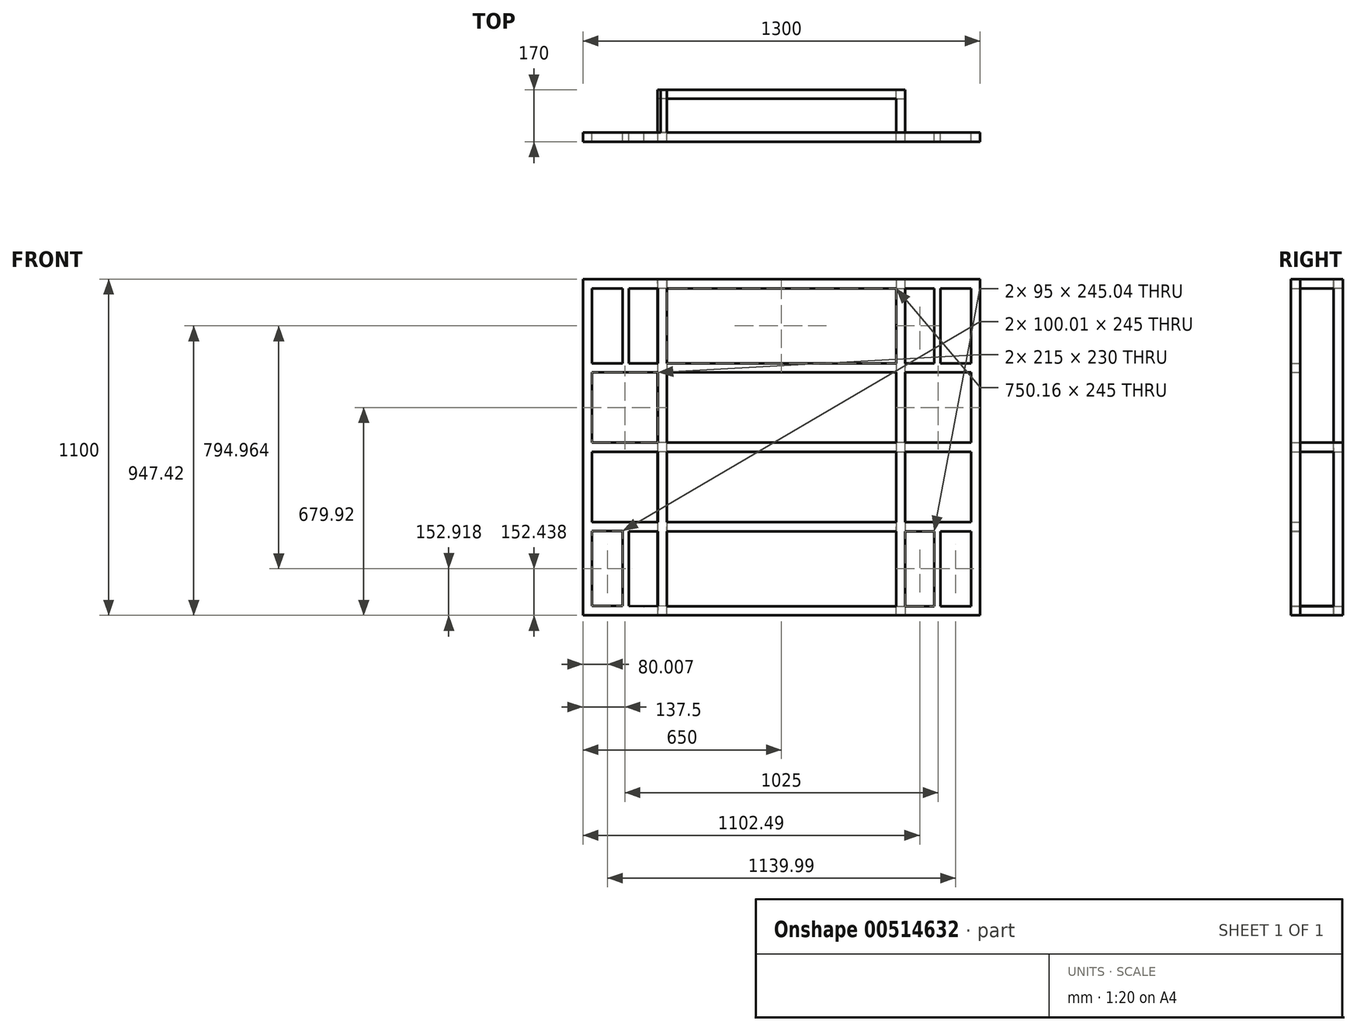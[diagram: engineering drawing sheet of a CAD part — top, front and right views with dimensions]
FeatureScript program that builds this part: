
annotation { "Feature Type Name" : "Feature", "Feature Type Description" : "" }
export const myFeature = defineFeature(function(context is Context, id is Id, definition is map)
    precondition{}
    {
        {
            var Q0;
            Q0=qCreatedBy(makeId("Front.planeOp"),FACE);
            var sketch = newSketch(context, id + "F0", { "sketchPlane" : qUnion([Q0])});
            skLineSegment(sketch, "E0", {"start": v(-619.99, -274.5) * mm, "end": v(-519.99, -274.5) * mm});
            skLineSegment(sketch, "E1.MirrorCS", {"start": v(499.99, -520) * mm, "end": v(499.99, -275) * mm});
            skLineSegment(sketch, "E2.MirrorCS", {"start": v(519.99, -275) * mm, "end": v(519.99, -520) * mm});
            skLineSegment(sketch, "E3.MirrorCS", {"start": v(519.99, 275) * mm, "end": v(519.99, 520) * mm});
            skLineSegment(sketch, "E4.MirrorCS", {"start": v(499.99, 520) * mm, "end": v(499.99, 275) * mm});
            skLineSegment(sketch, "E5", {"start": v(619.99, 275) * mm, "end": v(519.99, 275) * mm});
            skLineSegment(sketch, "E6", {"start": v(499.99, 275) * mm, "end": v(404.99, 274.96) * mm});
            skLineSegment(sketch, "E7", {"start": v(519.99, 520) * mm, "end": v(620, 520.08) * mm});
            skLineSegment(sketch, "E8", {"start": v(499.99, 520) * mm, "end": v(404.99, 520) * mm});
            skLineSegment(sketch, "E9", {"start": v(404.99, 520) * mm, "end": v(404.99, 274.96) * mm});
            skLineSegment(sketch, "E10", {"start": v(374.99, 520) * mm, "end": v(375.08, 275) * mm});
            skLineSegment(sketch, "E11", {"start": v(-519.99, 519.5) * mm, "end": v(-620, 519.59) * mm});
            skLineSegment(sketch, "E12.MirrorCS", {"start": v(404.99, -520) * mm, "end": v(404.99, -274.96) * mm});
            skLineSegment(sketch, "E13.MirrorCS", {"start": v(374.99, -520) * mm, "end": v(375.08, -275) * mm});
            skLineSegment(sketch, "E14.MirrorCS", {"start": v(-374.99, 520) * mm, "end": v(-375.08, 275) * mm});
            skLineSegment(sketch, "E15.MirrorCS", {"start": v(-404.99, 520) * mm, "end": v(-404.99, 274.96) * mm});
            skLineSegment(sketch, "E16.MirrorCS", {"start": v(-374.99, -520) * mm, "end": v(-375.08, -275) * mm});
            skLineSegment(sketch, "E17.MirrorCS", {"start": v(-404.99, -519.5) * mm, "end": v(-404.99, -274.96) * mm});
            skLineSegment(sketch, "E18", {"start": v(405, 245) * mm, "end": v(405, 15) * mm});
            skLineSegment(sketch, "E19", {"start": v(374.92, 245) * mm, "end": v(374.92, 15) * mm});
            skLineSegment(sketch, "E20", {"start": v(404.99, -245) * mm, "end": v(404.99, -15) * mm});
            skLineSegment(sketch, "E21", {"start": v(375.08, -245) * mm, "end": v(375.08, -15) * mm});
            skLineSegment(sketch, "E22.MirrorCS", {"start": v(-375.08, 245) * mm, "end": v(-375.08, 15) * mm});
            skLineSegment(sketch, "E23.MirrorCS", {"start": v(-405, 245) * mm, "end": v(-405, 15) * mm});
            skLineSegment(sketch, "E24.MirrorCS", {"start": v(-375.08, -245) * mm, "end": v(-375.08, -15) * mm});
            skLineSegment(sketch, "E25.MirrorCS", {"start": v(-404.99, -245) * mm, "end": v(-404.99, -15) * mm});
            skLineSegment(sketch, "E26", {"start": v(519.99, -275) * mm, "end": v(619.99, -275) * mm});
            skLineSegment(sketch, "E27", {"start": v(499.99, -275) * mm, "end": v(404.99, -274.96) * mm});
            skLineSegment(sketch, "E28", {"start": v(620, -519.92) * mm, "end": v(519.99, -520) * mm});
            skLineSegment(sketch, "E29", {"start": v(499.99, -520) * mm, "end": v(404.99, -520) * mm});
            skLineSegment(sketch, "E30", {"start": v(374.99, -520) * mm, "end": v(-374.99, -520) * mm});
            skLineSegment(sketch, "E31", {"start": v(-620, -519.42) * mm, "end": v(-519.99, -519.5) * mm});
            skLineSegment(sketch, "E32", {"start": v(-404.99, -274.96) * mm, "end": v(-499.99, -275) * mm});
            skLineSegment(sketch, "E33", {"start": v(-375.08, -275) * mm, "end": v(375.08, -275) * mm});
            skLineSegment(sketch, "E34", {"start": v(-620, -519.42) * mm, "end": v(-619.99, -274.5) * mm});
            skLineSegment(sketch, "E35", {"start": v(-620, -245) * mm, "end": v(-620, -15) * mm});
            skLineSegment(sketch, "E36", {"start": v(-620, 15) * mm, "end": v(-620, 245) * mm});
            skLineSegment(sketch, "E37", {"start": v(-619.99, 275) * mm, "end": v(-519.99, 274.5) * mm});
            skLineSegment(sketch, "E38", {"start": v(-499.99, 275) * mm, "end": v(-404.99, 274.96) * mm});
            skLineSegment(sketch, "E39", {"start": v(-375.08, 275) * mm, "end": v(375.08, 275) * mm});
            skLineSegment(sketch, "E40", {"start": v(-374.99, 520) * mm, "end": v(374.99, 520) * mm});
            skLineSegment(sketch, "E41", {"start": v(620, 520.08) * mm, "end": v(619.99, 275) * mm});
            skLineSegment(sketch, "E42", {"start": v(620, 245) * mm, "end": v(620, 15) * mm});
            skLineSegment(sketch, "E43", {"start": v(620, -15) * mm, "end": v(620, -245) * mm});
            skLineSegment(sketch, "E44", {"start": v(619.99, -275) * mm, "end": v(620, -519.92) * mm});
            skLineSegment(sketch, "E45", {"start": v(405, 15) * mm, "end": v(620, 15) * mm});
            skLineSegment(sketch, "E46", {"start": v(620, -15) * mm, "end": v(404.99, -15) * mm});
            skLineSegment(sketch, "E47", {"start": v(-620, 245) * mm, "end": v(-405, 245) * mm});
            skLineSegment(sketch, "E48", {"start": v(405, 245) * mm, "end": v(620, 245) * mm});
            skLineSegment(sketch, "E49", {"start": v(-375.08, 245) * mm, "end": v(374.92, 245) * mm});
            skLineSegment(sketch, "E50", {"start": v(-650, -549.92) * mm, "end": v(650, -549.92) * mm});
            skLineSegment(sketch, "E51", {"start": v(-650, 550.08) * mm, "end": v(-650, -549.92) * mm});
            skLineSegment(sketch, "E52", {"start": v(650, 550.08) * mm, "end": v(650, -549.92) * mm});
            skLineSegment(sketch, "E53", {"start": v(-620, -245) * mm, "end": v(-404.99, -245) * mm});
            skLineSegment(sketch, "E54", {"start": v(-375.08, -245) * mm, "end": v(375.08, -245) * mm});
            skLineSegment(sketch, "E55", {"start": v(404.99, -245) * mm, "end": v(620, -245) * mm});
            skLineSegment(sketch, "E56", {"start": v(-620, -15) * mm, "end": v(-404.99, -15) * mm});
            skLineSegment(sketch, "E57", {"start": v(-375.08, -15) * mm, "end": v(375.08, -15) * mm});
            skLineSegment(sketch, "E58", {"start": v(374.92, 15) * mm, "end": v(-375.08, 15) * mm});
            skLineSegment(sketch, "E59", {"start": v(-405, 15) * mm, "end": v(-620, 15) * mm});
            skLineSegment(sketch, "E60", {"start": v(-620, 519.59) * mm, "end": v(-620, 369.59) * mm});
            skLineSegment(sketch, "E61", {"start": v(-619.99, 275) * mm, "end": v(-620, 369.59) * mm});
            skLineSegment(sketch, "E62", {"start": v(-449.99, 370.08) * mm, "end": v(-449.99, 520.08) * mm});
            skLineSegment(sketch, "E63", {"start": v(-499.99, 519.5) * mm, "end": v(-449.99, 520.08) * mm});
            skLineSegment(sketch, "E64", {"start": v(-519.99, 519.5) * mm, "end": v(-499.99, 519.5) * mm});
            skLineSegment(sketch, "E65.MirrorCS", {"start": v(449.99, 370.08) * mm, "end": v(449.99, 520.08) * mm});
            skLineSegment(sketch, "E66.MirrorCS", {"start": v(519.99, 519.5) * mm, "end": v(499.99, 519.5) * mm});
            skLineSegment(sketch, "E67.MirrorCS", {"start": v(-449.99, -370.08) * mm, "end": v(-449.99, -520.08) * mm});
            skLineSegment(sketch, "E68.MirrorCS", {"start": v(449.99, -370.08) * mm, "end": v(449.99, -520.08) * mm});
            skLineSegment(sketch, "E69", {"start": v(-650, 550.08) * mm, "end": v(650, 550.08) * mm});
            skLineSegment(sketch, "E70", {"start": v(-449.99, 520.08) * mm, "end": v(-404.99, 520) * mm});
            skLineSegment(sketch, "E71", {"start": v(404.99, 520) * mm, "end": v(374.99, 520) * mm});
            skLineSegment(sketch, "E72", {"start": v(449.99, 370.08) * mm, "end": v(620, 370.08) * mm});
            skLineSegment(sketch, "E73", {"start": v(-449.99, 370.08) * mm, "end": v(-620, 369.59) * mm});
            skLineSegment(sketch, "E74", {"start": v(-499.99, 519.5) * mm, "end": v(-499.99, 275) * mm});
            skLineSegment(sketch, "E75", {"start": v(-519.99, 519.5) * mm, "end": v(-519.99, 274.5) * mm});
            skLineSegment(sketch, "E76", {"start": v(-449.99, -520.08) * mm, "end": v(-404.99, -519.5) * mm});
            skLineSegment(sketch, "E77", {"start": v(-519.99, -274.5) * mm, "end": v(-519.99, -519.5) * mm});
            skLineSegment(sketch, "E78", {"start": v(-499.99, -275) * mm, "end": v(-499.9, -519.5) * mm});
            skLineSegment(sketch, "E79", {"start": v(-499.9, -519.5) * mm, "end": v(-449.99, -520.08) * mm});
            skLineSegment(sketch, "E80", {"start": v(-449.99, -370.08) * mm, "end": v(-620, -370.08) * mm});
            skLineSegment(sketch, "E81", {"start": v(449.99, -370.08) * mm, "end": v(620, -370.08) * mm});
            skSolve(sketch);
        }
        {
            var Q0;
            Q0=makeQuery(id+"F0.imprint","IMPRINT",FACE,{"disambiguationData":[TD([[makeQuery(id+"F0.imprint","IMPRINT",EDGE,{"derivedFrom":sQuery(id+"F0.wireOp",EDGE,"E0")}),1.0]])]});
            var Q1;
            {var subQ9=sQuery(id+"F0.wireOp",EDGE,"E11");Q1=makeQuery(id+"F0.imprint","IMPRINT",FACE,{"disambiguationData":[TD([[makeQuery(id+"F0.imprint","IMPRINT",EDGE,{"derivedFrom":subQ9}),-1.0]])]});}
            var Q2;
            {var subQ0=sQuery(id+"F0.wireOp",EDGE,"E66.MirrorCS");Q2=makeQuery(id+"F0.imprint","IMPRINT",FACE,{"disambiguationData":[TD([[makeQuery(id+"F0.imprint","IMPRINT",EDGE,{"derivedFrom":subQ0}),1.0]])]});}
            var Q3;
            {var subQ0=sQuery(id+"F0.wireOp",EDGE,"E64");Q3=makeQuery(id+"F0.imprint","IMPRINT",FACE,{"disambiguationData":[TD([[makeQuery(id+"F0.imprint","IMPRINT",EDGE,{"derivedFrom":subQ0}),-1.0]])]});}
            extrude(context, id + "F1", {"entities" : qUnion([Q0, Q1, Q2, Q3]), "depth" : 30 * mm, "offsetDistance" : 25.4 * mm});
        }
        {
            var Q0;
            Q0=makeQuery(id+"F1.opExtrude","CAP_FACE",FACE,{"disambiguationData":[OSD([sQuery(id+"F0.wireOp",EDGE,"E0"),sQuery(id+"F0.wireOp",EDGE,"E1.MirrorCS"),sQuery(id+"F0.wireOp",EDGE,"E2.MirrorCS"),sQuery(id+"F0.wireOp",EDGE,"E3.MirrorCS"),sQuery(id+"F0.wireOp",EDGE,"E4.MirrorCS"),sQuery(id+"F0.wireOp",EDGE,"E5"),sQuery(id+"F0.wireOp",EDGE,"E6"),sQuery(id+"F0.wireOp",EDGE,"E7"),sQuery(id+"F0.wireOp",EDGE,"E8"),sQuery(id+"F0.wireOp",EDGE,"E9"),sQuery(id+"F0.wireOp",EDGE,"E10"),sQuery(id+"F0.wireOp",EDGE,"E11"),sQuery(id+"F0.wireOp",EDGE,"E12.MirrorCS"),sQuery(id+"F0.wireOp",EDGE,"E13.MirrorCS"),sQuery(id+"F0.wireOp",EDGE,"E14.MirrorCS"),sQuery(id+"F0.wireOp",EDGE,"E15.MirrorCS"),sQuery(id+"F0.wireOp",EDGE,"E16.MirrorCS"),sQuery(id+"F0.wireOp",EDGE,"E17.MirrorCS"),sQuery(id+"F0.wireOp",EDGE,"E18"),sQuery(id+"F0.wireOp",EDGE,"E19"),sQuery(id+"F0.wireOp",EDGE,"E20"),sQuery(id+"F0.wireOp",EDGE,"E21"),sQuery(id+"F0.wireOp",EDGE,"E22.MirrorCS"),sQuery(id+"F0.wireOp",EDGE,"E23.MirrorCS"),sQuery(id+"F0.wireOp",EDGE,"E24.MirrorCS"),sQuery(id+"F0.wireOp",EDGE,"E25.MirrorCS"),sQuery(id+"F0.wireOp",EDGE,"E26"),sQuery(id+"F0.wireOp",EDGE,"E27"),sQuery(id+"F0.wireOp",EDGE,"E28"),sQuery(id+"F0.wireOp",EDGE,"E29"),sQuery(id+"F0.wireOp",EDGE,"E30"),sQuery(id+"F0.wireOp",EDGE,"E31"),sQuery(id+"F0.wireOp",EDGE,"E32"),sQuery(id+"F0.wireOp",EDGE,"E33"),sQuery(id+"F0.wireOp",EDGE,"E34"),sQuery(id+"F0.wireOp",EDGE,"E35"),sQuery(id+"F0.wireOp",EDGE,"E36"),sQuery(id+"F0.wireOp",EDGE,"E37"),sQuery(id+"F0.wireOp",EDGE,"E38"),sQuery(id+"F0.wireOp",EDGE,"E39"),sQuery(id+"F0.wireOp",EDGE,"E40"),sQuery(id+"F0.wireOp",EDGE,"E41"),sQuery(id+"F0.wireOp",EDGE,"E42"),sQuery(id+"F0.wireOp",EDGE,"E43"),sQuery(id+"F0.wireOp",EDGE,"E44"),sQuery(id+"F0.wireOp",EDGE,"E45"),sQuery(id+"F0.wireOp",EDGE,"E46"),sQuery(id+"F0.wireOp",EDGE,"E47"),sQuery(id+"F0.wireOp",EDGE,"E48"),sQuery(id+"F0.wireOp",EDGE,"E49"),sQuery(id+"F0.wireOp",EDGE,"E50"),sQuery(id+"F0.wireOp",EDGE,"E51"),sQuery(id+"F0.wireOp",EDGE,"E52"),sQuery(id+"F0.wireOp",EDGE,"E53"),sQuery(id+"F0.wireOp",EDGE,"E54"),sQuery(id+"F0.wireOp",EDGE,"E55"),sQuery(id+"F0.wireOp",EDGE,"E56"),sQuery(id+"F0.wireOp",EDGE,"E57"),sQuery(id+"F0.wireOp",EDGE,"E58"),sQuery(id+"F0.wireOp",EDGE,"E59"),sQuery(id+"F0.wireOp",EDGE,"E60"),sQuery(id+"F0.wireOp",EDGE,"E61"),sQuery(id+"F0.wireOp",EDGE,"E63"),sQuery(id+"F0.wireOp",EDGE,"E69"),sQuery(id+"F0.wireOp",EDGE,"E70"),sQuery(id+"F0.wireOp",EDGE,"E74"),sQuery(id+"F0.wireOp",EDGE,"E75"),sQuery(id+"F0.wireOp",EDGE,"E76"),sQuery(id+"F0.wireOp",EDGE,"E77"),sQuery(id+"F0.wireOp",EDGE,"E78"),sQuery(id+"F0.wireOp",EDGE,"E79")])],"isStart":true});
            var sketch = newSketch(context, id + "F2", { "sketchPlane" : qUnion([Q0])});
            skLineSegment(sketch, "E82", {"start": v(374.99, -520) * mm, "end": v(404.99, -519.5) * mm});
            skLineSegment(sketch, "E83", {"start": v(404.99, -519.5) * mm, "end": v(405.5, -549.92) * mm});
            skLineSegment(sketch, "E84", {"start": v(405.5, -549.92) * mm, "end": v(374.99, -550.42) * mm});
            skLineSegment(sketch, "E85", {"start": v(374.99, -550.42) * mm, "end": v(374.99, -520) * mm});
            skLineSegment(sketch, "E86", {"start": v(-374.99, -520) * mm, "end": v(-404.99, -520) * mm});
            skLineSegment(sketch, "E87", {"start": v(-404.99, -520) * mm, "end": v(-404.99, -549.92) * mm});
            skLineSegment(sketch, "E88", {"start": v(-404.99, -549.92) * mm, "end": v(-374.99, -549.92) * mm});
            skLineSegment(sketch, "E89", {"start": v(-374.99, -549.92) * mm, "end": v(-374.99, -520) * mm});
            skLineSegment(sketch, "E90.MirrorCS", {"start": v(-374.99, 549.92) * mm, "end": v(-374.99, 520) * mm});
            skLineSegment(sketch, "E91.MirrorCS", {"start": v(-404.99, 520) * mm, "end": v(-404.99, 549.92) * mm});
            skLineSegment(sketch, "E92.MirrorCS", {"start": v(-404.99, 549.92) * mm, "end": v(-374.99, 549.92) * mm});
            skLineSegment(sketch, "E93.MirrorCS", {"start": v(-374.99, 520) * mm, "end": v(-404.99, 520) * mm});
            skLineSegment(sketch, "E94.MirrorCS", {"start": v(374.99, 520) * mm, "end": v(404.99, 519.5) * mm});
            skLineSegment(sketch, "E95.MirrorCS", {"start": v(374.99, 550.42) * mm, "end": v(374.99, 520) * mm});
            skLineSegment(sketch, "E96.MirrorCS", {"start": v(405.5, 549.92) * mm, "end": v(374.99, 550.42) * mm});
            skLineSegment(sketch, "E97.MirrorCS", {"start": v(404.99, 519.5) * mm, "end": v(405.5, 549.92) * mm});
            skLineSegment(sketch, "E98", {"start": v(-405, 15) * mm, "end": v(-374.92, 15) * mm});
            skLineSegment(sketch, "E99", {"start": v(-374.92, 15) * mm, "end": v(-375.08, -15) * mm});
            skLineSegment(sketch, "E100", {"start": v(-375.08, -15) * mm, "end": v(-404.99, -15) * mm});
            skLineSegment(sketch, "E101", {"start": v(-404.99, -15) * mm, "end": v(-405, 15) * mm});
            skLineSegment(sketch, "E102", {"start": v(375.08, 15) * mm, "end": v(375.08, -15) * mm});
            skLineSegment(sketch, "E103", {"start": v(375.08, -15) * mm, "end": v(404.99, -15) * mm});
            skLineSegment(sketch, "E104", {"start": v(404.99, -15) * mm, "end": v(405, 15) * mm});
            skLineSegment(sketch, "E105", {"start": v(405, 15) * mm, "end": v(375.08, 15) * mm});
            skLineSegment(sketch, "E106", {"start": v(-374.99, -520) * mm, "end": v(374.99, -520) * mm});
            skLineSegment(sketch, "E107", {"start": v(374.99, -550.42) * mm, "end": v(-374.99, -549.92) * mm});
            skLineSegment(sketch, "E108", {"start": v(-375.08, -15) * mm, "end": v(375.08, -15) * mm});
            skLineSegment(sketch, "E109", {"start": v(375.08, 15) * mm, "end": v(-374.92, 15) * mm});
            skLineSegment(sketch, "E110", {"start": v(-375.08, -15) * mm, "end": v(-374.99, -520) * mm});
            skLineSegment(sketch, "E111", {"start": v(-404.99, -15) * mm, "end": v(-404.99, -520) * mm});
            skLineSegment(sketch, "E112", {"start": v(374.99, -520) * mm, "end": v(375.08, -15) * mm});
            skLineSegment(sketch, "E113", {"start": v(404.99, -519.5) * mm, "end": v(404.99, -15) * mm});
            skLineSegment(sketch, "E114", {"start": v(405, 15) * mm, "end": v(404.99, 520) * mm});
            skLineSegment(sketch, "E115", {"start": v(375.08, 15) * mm, "end": v(374.99, 520) * mm});
            skLineSegment(sketch, "E116", {"start": v(-374.92, 15) * mm, "end": v(-374.99, 520) * mm});
            skLineSegment(sketch, "E117", {"start": v(-404.99, 520) * mm, "end": v(-405, 15) * mm});
            skLineSegment(sketch, "E118", {"start": v(-374.99, 549.92) * mm, "end": v(374.99, 550.42) * mm});
            skLineSegment(sketch, "E119", {"start": v(374.99, 520) * mm, "end": v(-374.99, 520) * mm});
            skSolve(sketch);
        }
        {
            var Q0;
            Q0=makeQuery(id+"F2.imprint","IMPRINT",FACE,{"disambiguationData":[TD([[makeQuery(id+"F2.imprint","IMPRINT",EDGE,{"derivedFrom":sQuery(id+"F2.wireOp",EDGE,"E86")}),1.0]])]});
            var Q1;
            {var subQ0=sQuery(id+"F2.wireOp",EDGE,"E82");Q1=makeQuery(id+"F2.imprint","IMPRINT",FACE,{"disambiguationData":[TD([[makeQuery(id+"F2.imprint","IMPRINT",EDGE,{"derivedFrom":subQ0}),-1.0]])]});}
            var Q2;
            Q2=makeQuery(id+"F2.imprint","IMPRINT",FACE,{"disambiguationData":[TD([[makeQuery(id+"F2.imprint","IMPRINT",EDGE,{"derivedFrom":sQuery(id+"F2.wireOp",EDGE,"E102")}),1.0]])]});
            var Q3;
            {var subQ8=sQuery(id+"F2.wireOp",EDGE,"E94.MirrorCS");Q3=makeQuery(id+"F2.imprint","IMPRINT",FACE,{"disambiguationData":[TD([[makeQuery(id+"F2.imprint","IMPRINT",EDGE,{"derivedFrom":subQ8}),1.0]])]});}
            var Q4;
            Q4=makeQuery(id+"F2.imprint","IMPRINT",FACE,{"disambiguationData":[TD([[makeQuery(id+"F2.imprint","IMPRINT",EDGE,{"derivedFrom":sQuery(id+"F2.wireOp",EDGE,"E90.MirrorCS")}),-1.0]])]});
            var Q5;
            Q5=makeQuery(id+"F2.imprint","IMPRINT",FACE,{"disambiguationData":[TD([[makeQuery(id+"F2.imprint","IMPRINT",EDGE,{"derivedFrom":sQuery(id+"F2.wireOp",EDGE,"E98")}),-1.0]])]});
            extrude(context, id + "F3", {"entities" : qUnion([Q0, Q1, Q2, Q3, Q4, Q5]), "operationType" : NewBodyOperationType.ADD, "depth" : 140 * mm, "offsetDistance" : 25.4 * mm});
        }
        {
            var Q0;
            Q0=makeQuery(id+"F3.opExtrude","SWEPT_FACE",FACE,{"disambiguationData":[OSD([sQuery(id+"F2.wireOp",EDGE,"E86")])]});
            var sketch = newSketch(context, id + "F4", { "sketchPlane" : qUnion([Q0])});
            skLineSegment(sketch, "E120.bottom", {"start": v(374.99, 140) * mm, "end": v(404.99, 140) * mm});
            skLineSegment(sketch, "E120.top", {"start": v(374.99, 110) * mm, "end": v(404.99, 110) * mm});
            skLineSegment(sketch, "E120.left", {"start": v(374.99, 140) * mm, "end": v(374.99, 110) * mm});
            skLineSegment(sketch, "E120.right", {"start": v(404.99, 140) * mm, "end": v(404.99, 110) * mm});
            skSolve(sketch);
        }
        {
            var Q0;
            Q0=makeQuery(id+"F4.imprint","IMPRINT",FACE,{"disambiguationData":[TD([[makeQuery(id+"F4.imprint","IMPRINT",EDGE,{"derivedFrom":sQuery(id+"F4.wireOp",EDGE,"E120.bottom")}),-1.0]])]});
            extrude(context, id + "F5", {"entities" : qUnion([Q0]), "operationType" : NewBodyOperationType.ADD, "depth" : 1069.34 * mm, "offsetDistance" : 25.4 * mm});
        }
        {
            var Q0;
            Q0=makeQuery(id+"F5.boolean.opBoolean","MERGE",FACE,{"derivedFrom":[makeQuery(id+"F3.opExtrude","SWEPT_FACE",FACE,{"disambiguationData":[OSD([sQuery(id+"F2.wireOp",EDGE,"E90.MirrorCS")])]}),makeQuery(id+"F5.opExtrude","SWEPT_FACE",FACE,{"disambiguationData":[OSD([sQuery(id+"F4.wireOp",EDGE,"E120.left")])]})]});
            var sketch = newSketch(context, id + "F6", { "sketchPlane" : qUnion([Q0])});
            skLineSegment(sketch, "E121.bottom", {"start": v(-140, 549.92) * mm, "end": v(-110, 549.92) * mm});
            skLineSegment(sketch, "E121.top", {"start": v(-140, 520) * mm, "end": v(-110, 520) * mm});
            skLineSegment(sketch, "E121.left", {"start": v(-140, 549.92) * mm, "end": v(-140, 520) * mm});
            skLineSegment(sketch, "E121.right", {"start": v(-110, 549.92) * mm, "end": v(-110, 520) * mm});
            skSolve(sketch);
        }
        {
            var Q0;
            Q0=makeQuery(id+"F6.imprint","IMPRINT",FACE,{"disambiguationData":[TD([[makeQuery(id+"F6.imprint","IMPRINT",EDGE,{"derivedFrom":sQuery(id+"F6.wireOp",EDGE,"E121.bottom")}),-1.0]])]});
            extrude(context, id + "F7", {"entities" : qUnion([Q0]), "operationType" : NewBodyOperationType.ADD, "depth" : 777.75 * mm, "offsetDistance" : 25.4 * mm});
        }
        {
            var Q0;
            Q0=makeQuery(id+"F3.opExtrude","SWEPT_FACE",FACE,{"disambiguationData":[OSD([sQuery(id+"F2.wireOp",EDGE,"E102")])]});
            var sketch = newSketch(context, id + "F8", { "sketchPlane" : qUnion([Q0])});
            skLineSegment(sketch, "E122.bottom", {"start": v(140, 15) * mm, "end": v(110, 15) * mm});
            skLineSegment(sketch, "E122.top", {"start": v(140, -15) * mm, "end": v(110, -15) * mm});
            skLineSegment(sketch, "E122.left", {"start": v(140, 15) * mm, "end": v(140, -15) * mm});
            skLineSegment(sketch, "E122.right", {"start": v(110, 15) * mm, "end": v(110, -15) * mm});
            skSolve(sketch);
        }
        {
            var Q0;
            Q0=makeQuery(id+"F8.imprint","IMPRINT",FACE,{"disambiguationData":[TD([[makeQuery(id+"F8.imprint","IMPRINT",EDGE,{"derivedFrom":sQuery(id+"F8.wireOp",EDGE,"E122.bottom")}),1.0]])]});
            extrude(context, id + "F9", {"entities" : qUnion([Q0]), "operationType" : NewBodyOperationType.ADD, "depth" : 779.78 * mm, "offsetDistance" : 25.4 * mm});
        }
        {
            var Q0;
            {var subQ0=sQuery(id+"F0.wireOp",EDGE,"E50");Q0=makeQuery(id+"F3.boolean.opBoolean","MERGE",FACE,{"derivedFrom":[makeQuery(id+"F1.opExtrude","SWEPT_FACE",FACE,{"disambiguationData":[OSD([subQ0])]}),makeQuery(id+"F3.opExtrude","SWEPT_FACE",FACE,{"disambiguationData":[OSD([sQuery(id+"F2.wireOp",EDGE,"E88")])]}),makeQuery(id+"F3.opExtrude","SWEPT_FACE",FACE,{"disambiguationData":[OSD([subQ0])]})]});}
            var sketch = newSketch(context, id + "F10", { "sketchPlane" : qUnion([Q0])});
            skLineSegment(sketch, "E123.bottom", {"start": v(-405.5, -140) * mm, "end": v(-374.99, -140) * mm});
            skLineSegment(sketch, "E123.top", {"start": v(-405.5, -110) * mm, "end": v(-374.99, -110) * mm});
            skLineSegment(sketch, "E123.left", {"start": v(-405.5, -140) * mm, "end": v(-405.5, -110) * mm});
            skLineSegment(sketch, "E123.right", {"start": v(-374.99, -140) * mm, "end": v(-374.99, -110) * mm});
            skSolve(sketch);
        }
        {
            var Q0;
            Q0=makeQuery(id+"F10.imprint","IMPRINT",FACE,{"disambiguationData":[TD([[makeQuery(id+"F10.imprint","IMPRINT",EDGE,{"derivedFrom":sQuery(id+"F10.wireOp",EDGE,"E123.bottom")}),1.0]])]});
            extrude(context, id + "F11", {"entities" : qUnion([Q0]), "operationType" : NewBodyOperationType.ADD, "oppositeDirection" : true, "depth" : 1099.82 * mm, "offsetDistance" : 25.4 * mm});
        }
        {
            var Q0;
            Q0=makeQuery(id+"F11.opExtrude","SWEPT_FACE",FACE,{"disambiguationData":[OSD([sQuery(id+"F10.wireOp",EDGE,"E123.left")])]});
            var sketch = newSketch(context, id + "F12", { "sketchPlane" : qUnion([Q0])});
            skLineSegment(sketch, "E124.bottom", {"start": v(-140, -549.92) * mm, "end": v(-110, -549.92) * mm});
            skLineSegment(sketch, "E124.top", {"start": v(-140, -519.91) * mm, "end": v(-110, -519.91) * mm});
            skLineSegment(sketch, "E124.left", {"start": v(-140, -549.92) * mm, "end": v(-140, -519.91) * mm});
            skLineSegment(sketch, "E124.right", {"start": v(-110, -549.92) * mm, "end": v(-110, -519.91) * mm});
            skSolve(sketch);
        }
        {
            var Q0;
            Q0=makeQuery(id+"F12.imprint","IMPRINT",FACE,{"disambiguationData":[TD([[makeQuery(id+"F12.imprint","IMPRINT",EDGE,{"derivedFrom":sQuery(id+"F12.wireOp",EDGE,"E124.bottom")}),1.0]])]});
            extrude(context, id + "F13", {"entities" : qUnion([Q0]), "operationType" : NewBodyOperationType.ADD, "oppositeDirection" : true, "depth" : 810.26 * mm, "offsetDistance" : 25.4 * mm});
        }
    });
